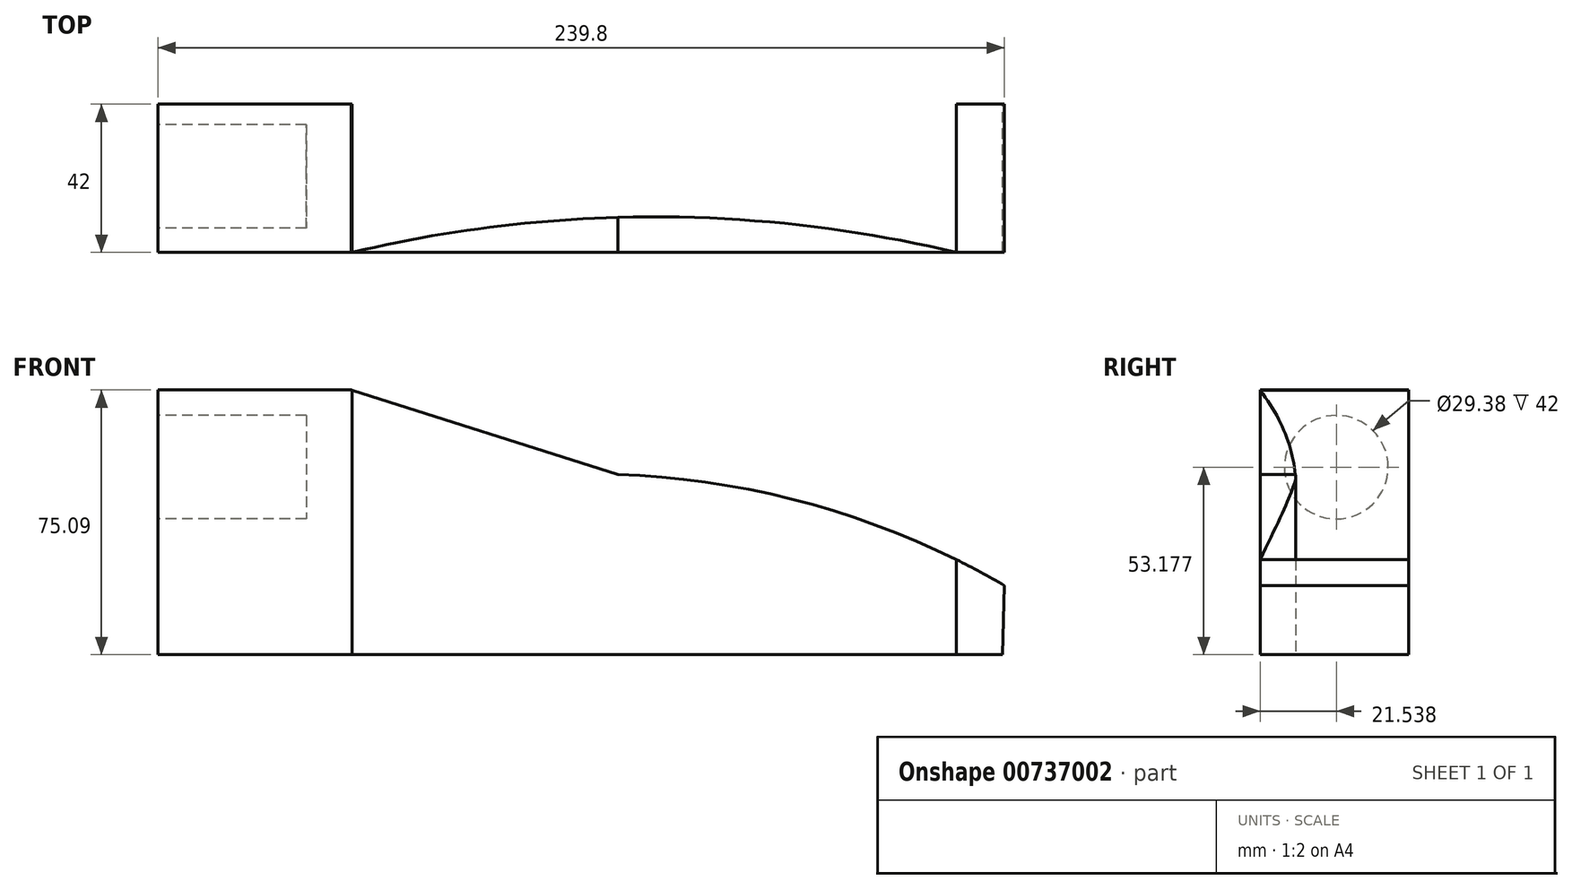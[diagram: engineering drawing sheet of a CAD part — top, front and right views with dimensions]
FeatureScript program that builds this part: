
annotation { "Feature Type Name" : "Feature", "Feature Type Description" : "" }
export const myFeature = defineFeature(function(context is Context, id is Id, definition is map)
    precondition{}
    {
        {
            var Q0;
            Q0=qCreatedBy(makeId("Top.planeOp"),FACE);
            var sketch = newSketch(context, id + "F0", { "sketchPlane" : qUnion([Q0])});
            skLineSegment(sketch, "E0.bottom", {"start": v(-12.02, 36.26) * mm, "end": v(42.98, 36.26) * mm});
            skLineSegment(sketch, "E0.top", {"start": v(-12.02, -5.74) * mm, "end": v(42.98, -5.74) * mm});
            skLineSegment(sketch, "E0.left", {"start": v(-12.02, 36.26) * mm, "end": v(-12.02, -5.74) * mm});
            skLineSegment(sketch, "E0.right", {"start": v(227.98, 26.26) * mm, "end": v(227.98, 4.26) * mm});
            skPoint(sketch, "E1.visualSharp", {"position": v(227.98, 36.26) * mm});
            skPoint(sketch, "E2.visualSharp", {"position": v(227.98, -5.74) * mm});
            skLineSegment(sketch, "E3.0", {"start": v(42.98, 36.26) * mm, "end": v(42.98, -5.74) * mm});
            skArc(sketch, "E4", {"start": v(217.98, -5.74) * mm, "mid": v(130.48, 9.14) * mm, "end": v(42.98, -5.74) * mm});
            skArc(sketch, "E5.MirrorCS", {"start": v(217.98, 36.26) * mm, "mid": v(130.48, 21.38) * mm, "end": v(42.98, 36.26) * mm});
            skLineSegment(sketch, "E6", {"start": v(42.98, 36.26) * mm, "end": v(217.98, 36.26) * mm});
            skLineSegment(sketch, "E7", {"start": v(42.98, -5.74) * mm, "end": v(217.98, -5.74) * mm});
            skLineSegment(sketch, "E8", {"start": v(227.98, 26.26) * mm, "end": v(227.98, 36.26) * mm});
            skLineSegment(sketch, "E9", {"start": v(227.98, 36.26) * mm, "end": v(217.98, 36.26) * mm});
            skLineSegment(sketch, "E10", {"start": v(217.98, -5.74) * mm, "end": v(227.98, -5.74) * mm});
            skLineSegment(sketch, "E11", {"start": v(227.98, 4.26) * mm, "end": v(227.98, -5.74) * mm});
            skSolve(sketch);
        }
        {
            var Q0;
            Q0=makeQuery(id+"F0.imprint","IMPRINT",FACE,{"disambiguationData":[TD([[makeQuery(id+"F0.imprint","IMPRINT",EDGE,{"derivedFrom":sQuery(id+"F0.wireOp",EDGE,"E0.bottom")}),-1.0]])]});
            var Q1;
            Q1=makeQuery(id+"F0.imprint","IMPRINT",FACE,{"disambiguationData":[TD([[makeQuery(id+"F0.imprint","IMPRINT",EDGE,{"derivedFrom":sQuery(id+"F0.wireOp",EDGE,"E0.right")}),-1.0]])]});
            var Q2;
            Q2=makeQuery(id+"F0.imprint","IMPRINT",FACE,{"disambiguationData":[TD([[makeQuery(id+"F0.imprint","IMPRINT",EDGE,{"derivedFrom":sQuery(id+"F0.wireOp",EDGE,"E5.MirrorCS")}),-1.0]])]});
            var Q3;
            Q3=makeQuery(id+"F0.imprint","IMPRINT",FACE,{"disambiguationData":[TD([[makeQuery(id+"F0.imprint","IMPRINT",EDGE,{"derivedFrom":sQuery(id+"F0.wireOp",EDGE,"E4")}),1.0]])]});
            extrude(context, id + "F1", {"entities" : qUnion([Q0, Q1, Q2, Q3]), "depth" : 75 * mm, "offsetDistance" : 25.4 * mm});
        }
        {
            var Q0;
            Q0=qCreatedBy(makeId("Front.planeOp"),FACE);
            var sketch = newSketch(context, id + "F2", { "sketchPlane" : qUnion([Q0])});
            skArc(sketch, "E12", {"start": v(228.2, 19.66) * mm, "mid": v(175.35, 42.14) * mm, "end": v(118.63, 51.12) * mm});
            skLineSegment(sketch, "E13", {"start": v(43.16, 75.09) * mm, "end": v(-11.61, 75.09) * mm});
            skLineSegment(sketch, "E14", {"start": v(-11.61, 75.09) * mm, "end": v(-11.61, 0) * mm});
            skLineSegment(sketch, "E15", {"start": v(227.7, 0) * mm, "end": v(-11.61, 0) * mm});
            skLineSegment(sketch, "E16", {"start": v(228.2, 19.66) * mm, "end": v(227.7, 0) * mm});
            skLineSegment(sketch, "E17", {"start": v(43.16, 75.09) * mm, "end": v(118.63, 51.12) * mm});
            skSolve(sketch);
        }
        {
            var Q0;
            Q0=makeQuery(id+"F1.opExtrude","SWEPT_FACE",FACE,{"disambiguationData":[OSD([sQuery(id+"F0.wireOp",EDGE,"E0.top"),sQuery(id+"F0.wireOp",EDGE,"E7"),sQuery(id+"F0.wireOp",EDGE,"E10")])]});
            extrude(context, id + "F3", {"entities" : qUnion([Q0]), "operationType" : NewBodyOperationType.REMOVE, "oppositeDirection" : true, "depth" : 101.6 * mm, "offsetDistance" : 25.4 * mm});
        }
        {
            var Q0;
            Q0=makeQuery(id+"F2.imprint","IMPRINT",FACE,{"disambiguationData":[TD([[makeQuery(id+"F2.imprint","IMPRINT",EDGE,{"derivedFrom":sQuery(id+"F2.wireOp",EDGE,"E12")}),1.0]])]});
            extrude(context, id + "F4", {"entities" : qUnion([Q0]), "depth" : 42 * mm, "offsetDistance" : 25.4 * mm});
        }
        {
            var Q0;
            Q0=makeQuery(id+"F4.opExtrude","SWEPT_FACE",FACE,{"disambiguationData":[OSD([sQuery(id+"F2.wireOp",EDGE,"E15")])]});
            var sketch = newSketch(context, id + "F5", { "sketchPlane" : qUnion([Q0])});
            skLineSegment(sketch, "E18.0", {"start": v(43.39, 42) * mm, "end": v(43.39, 0) * mm});
            skLineSegment(sketch, "E19", {"start": v(214.55, 42) * mm, "end": v(214.55, 0) * mm});
            skArc(sketch, "E20", {"start": v(214.55, 0) * mm, "mid": v(128.97, 10.06) * mm, "end": v(43.39, 0) * mm});
            skArc(sketch, "E21.MirrorCS", {"start": v(214.55, 42) * mm, "mid": v(128.97, 31.94) * mm, "end": v(43.39, 42) * mm});
            skSolve(sketch);
        }
        {
            var Q0;
            {var subQ0=sQuery(id+"F5.wireOp",EDGE,"E20");Q0=makeQuery(id+"F5.imprint","IMPRINT",FACE,{"disambiguationData":[TD([[makeQuery(id+"F5.imprint","IMPRINT",EDGE,{"derivedFrom":subQ0}),1.0]])]});}
            extrude(context, id + "F6", {"entities" : qUnion([Q0]), "operationType" : NewBodyOperationType.REMOVE, "oppositeDirection" : true, "depth" : 127 * mm, "offsetDistance" : 25.4 * mm});
        }
        {
            var Q0;
            {var subQ0=sQuery(id+"F5.wireOp",EDGE,"E21.MirrorCS");Q0=makeQuery(id+"F5.imprint","IMPRINT",FACE,{"disambiguationData":[TD([[makeQuery(id+"F5.imprint","IMPRINT",EDGE,{"derivedFrom":subQ0}),-1.0]])]});}
            extrude(context, id + "F7", {"entities" : qUnion([Q0]), "operationType" : NewBodyOperationType.REMOVE, "oppositeDirection" : true, "depth" : 127 * mm, "offsetDistance" : 25.4 * mm});
        }
        {
            var Q0;
            Q0=makeQuery(id+"F4.opExtrude","SWEPT_FACE",FACE,{"disambiguationData":[OSD([sQuery(id+"F2.wireOp",EDGE,"E14")])]});
            var sketch = newSketch(context, id + "F8", { "sketchPlane" : qUnion([Q0])});
            skCircle(sketch, "E22", {"center": v(20.46, 53.18) * mm, "radius": 14.69 * mm});
            skSolve(sketch);
        }
        {
            var Q0;
            Q0=makeQuery(id+"F8.imprint","IMPRINT",FACE,{"disambiguationData":[TD([[makeQuery(id+"F8.imprint","IMPRINT",EDGE,{"derivedFrom":sQuery(id+"F8.wireOp",EDGE,"E22")}),1.0]])]});
            extrude(context, id + "F9", {"entities" : qUnion([Q0]), "operationType" : NewBodyOperationType.REMOVE, "oppositeDirection" : true, "depth" : 42 * mm, "offsetDistance" : 25.4 * mm});
        }
    });
